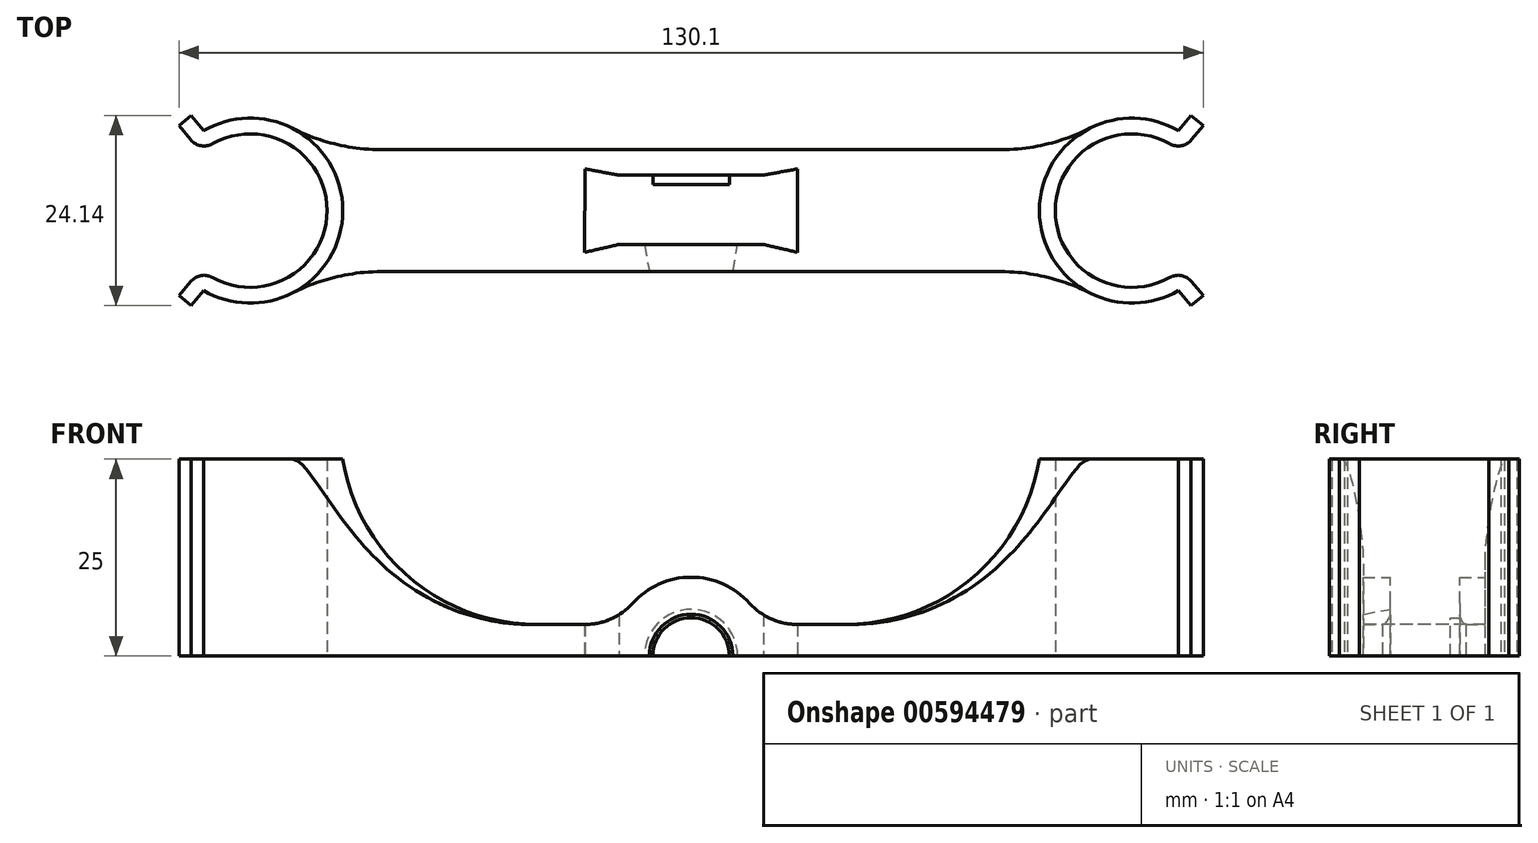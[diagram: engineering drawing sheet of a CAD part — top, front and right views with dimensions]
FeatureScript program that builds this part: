
annotation { "Feature Type Name" : "Feature", "Feature Type Description" : "" }
export const myFeature = defineFeature(function(context is Context, id is Id, definition is map)
    precondition{}
    {
        {
            var Q0;
            Q0=qCreatedBy(makeId("Top.planeOp"),FACE);
            var sketch = newSketch(context, id + "F0", { "sketchPlane" : qUnion([Q0])});
            skArc(sketch, "E0", {"start": v(-62.27, -7.47) * mm, "mid": v(-46.25, 0) * mm, "end": v(-62.27, 7.47) * mm});
            skLineSegment(sketch, "E1", {"start": v(-56, 0) * mm, "end": v(-68.54, -14.94) * mm, "construction": true});
            skLineSegment(sketch, "E2", {"start": v(-56, 0) * mm, "end": v(-67.56, 13.78) * mm, "construction": true});
            skArc(sketch, "E3", {"start": v(-63.55, -9) * mm, "mid": v(-44.25, 0) * mm, "end": v(-63.55, 9) * mm});
            skLineSegment(sketch, "E4", {"start": v(-63.55, 9) * mm, "end": v(-65.05, 10.78) * mm});
            skLineSegment(sketch, "E5", {"start": v(-65.05, 10.78) * mm, "end": v(-63.52, 12.07) * mm});
            skLineSegment(sketch, "E6", {"start": v(-63.52, 12.07) * mm, "end": v(-61.91, 10.16) * mm});
            skLineSegment(sketch, "E7", {"start": v(-54.18, 11.6) * mm, "end": v(-54.49, 9.63) * mm, "construction": true});
            skArc(sketch, "E8", {"start": v(-63.55, 9) * mm, "mid": v(-62.26, 8.25) * mm, "end": v(-60.78, 8.5) * mm});
            skLineSegment(sketch, "E9", {"start": v(-63.55, -9) * mm, "end": v(-65.05, -10.78) * mm});
            skLineSegment(sketch, "E10", {"start": v(-65.05, -10.78) * mm, "end": v(-63.52, -12.07) * mm});
            skLineSegment(sketch, "E11", {"start": v(-63.52, -12.07) * mm, "end": v(-61.91, -10.16) * mm});
            skArc(sketch, "E12", {"start": v(-60.78, -8.5) * mm, "mid": v(-62.26, -8.25) * mm, "end": v(-63.55, -9) * mm});
            skLineSegment(sketch, "E13.MirrorCS", {"start": v(65.05, -10.78) * mm, "end": v(63.52, -12.07) * mm});
            skLineSegment(sketch, "E14.MirrorCS", {"start": v(63.55, 9) * mm, "end": v(65.05, 10.78) * mm});
            skLineSegment(sketch, "E15.MirrorCS", {"start": v(63.52, -12.07) * mm, "end": v(61.91, -10.16) * mm});
            skLineSegment(sketch, "E16.MirrorCS", {"start": v(63.55, -9) * mm, "end": v(65.05, -10.78) * mm});
            skLineSegment(sketch, "E17.MirrorCS", {"start": v(65.05, 10.78) * mm, "end": v(63.52, 12.07) * mm});
            skLineSegment(sketch, "E18.MirrorCS", {"start": v(63.52, 12.07) * mm, "end": v(61.91, 10.16) * mm});
            skArc(sketch, "E19.MirrorCS", {"start": v(60.78, -8.5) * mm, "mid": v(62.26, -8.25) * mm, "end": v(63.55, -9) * mm});
            skArc(sketch, "E20.MirrorCS", {"start": v(63.55, 9) * mm, "mid": v(62.26, 8.25) * mm, "end": v(60.78, 8.5) * mm});
            skLineSegment(sketch, "E21.MirrorCS", {"start": v(54.18, 11.6) * mm, "end": v(54.49, 9.63) * mm, "construction": true});
            skArc(sketch, "E22.MirrorCS", {"start": v(62.27, -7.47) * mm, "mid": v(46.25, 0) * mm, "end": v(62.27, 7.47) * mm});
            skLineSegment(sketch, "E23.MirrorCS", {"start": v(56, 0) * mm, "end": v(68.54, -14.94) * mm, "construction": true});
            skLineSegment(sketch, "E24.MirrorCS", {"start": v(56, 0) * mm, "end": v(67.56, 13.78) * mm, "construction": true});
            skArc(sketch, "E25.MirrorCS", {"start": v(63.55, -9) * mm, "mid": v(44.25, 0) * mm, "end": v(63.55, 9) * mm});
            skSolve(sketch);
        }
        {
            var Q0;
            Q0=qSketchRegion(id+"F0",true);
            extrude(context, id + "F1", {"entities" : qUnion([Q0]), "depth" : 25 * mm});
        }
        {
            var Q0;
            Q0=qCreatedBy(makeId("Top.planeOp"),FACE);
            var sketch = newSketch(context, id + "F2", { "sketchPlane" : qUnion([Q0])});
            skLineSegment(sketch, "E26.bottom", {"start": v(50.08, -7.75) * mm, "end": v(-50.08, -7.75) * mm});
            skLineSegment(sketch, "E26.top", {"start": v(50.08, 7.75) * mm, "end": v(-50.08, 7.75) * mm});
            skLineSegment(sketch, "E26.left", {"start": v(50.08, -7.75) * mm, "end": v(50.08, 7.75) * mm});
            skLineSegment(sketch, "E26.right", {"start": v(-50.08, -7.75) * mm, "end": v(-50.08, 7.75) * mm});
            skPoint(sketch, "E26.middle", {"position": v(0, 0) * mm});
            skSolve(sketch);
        }
        {
            var Q0;
            Q0=qSketchRegion(id+"F2",true);
            extrude(context, id + "F3", {"entities" : qUnion([Q0]), "operationType" : NewBodyOperationType.ADD, "depth" : 4 * mm});
        }
        {
            var Q0;
            Q0=qCreatedBy(makeId("Top.planeOp"),FACE);
            var sketch = newSketch(context, id + "F4", { "sketchPlane" : qUnion([Q0])});
            skArc(sketch, "E27.0", {"start": v(-62.27, -7.47) * mm, "mid": v(-46.25, 0) * mm, "end": v(-62.27, 7.47) * mm});
            skArc(sketch, "E27.1", {"start": v(62.27, -7.47) * mm, "mid": v(46.25, 0) * mm, "end": v(62.27, 7.47) * mm});
            skLineSegment(sketch, "E28", {"start": v(-62.27, 7.47) * mm, "end": v(-62.27, -7.47) * mm});
            skLineSegment(sketch, "E29", {"start": v(62.27, 7.47) * mm, "end": v(62.27, -7.47) * mm});
            skSolve(sketch);
        }
        {
            var Q0;
            Q0=qSketchRegion(id+"F4",true);
            extrude(context, id + "F5", {"entities" : qUnion([Q0]), "operationType" : NewBodyOperationType.REMOVE, "endBound" : BoundingType.THROUGH_ALL, "depth" : 25 * mm});
        }
        {
            var Q0;
            Q0=qCreatedBy(makeId("Front.planeOp"),FACE);
            var sketch = newSketch(context, id + "F6", { "sketchPlane" : qUnion([Q0])});
            skArc(sketch, "E30", {"start": v(10, 0) * mm, "mid": v(0, 10) * mm, "end": v(-10, 0) * mm});
            skLineSegment(sketch, "E31.0", {"start": v(47.17, 0) * mm, "end": v(-47.17, 0) * mm});
            skSolve(sketch);
        }
        {
            var Q0;
            Q0=qSketchRegion(id+"F6",true);
            var Q1;
            Q1=makeQuery(id+"F3.opExtrude","SWEPT_FACE",FACE,{"disambiguationData":[OSD([sQuery(id+"F2.wireOp",EDGE,"E26.bottom")])]});
            var Q2;
            Q2=makeQuery(id+"F3.opExtrude","SWEPT_FACE",FACE,{"disambiguationData":[OSD([sQuery(id+"F2.wireOp",EDGE,"E26.top")])]});
            extrude(context, id + "F7", {"entities" : qUnion([Q0]), "operationType" : NewBodyOperationType.ADD, "endBound" : BoundingType.UP_TO_SURFACE, "endBoundEntityFace" : qUnion([Q1]), "depth" : 25 * mm, "hasSecondDirection" : true, "secondDirectionBound" : SecondDirectionBoundingType.UP_TO_SURFACE, "secondDirectionOppositeDirection" : true, "secondDirectionBoundEntityFace" : qUnion([Q2]), "secondDirectionDepth" : 25 * mm});
        }
        {
            var Q0;
            Q0=qCreatedBy(makeId("Top.planeOp"),FACE);
            var sketch = newSketch(context, id + "F8", { "sketchPlane" : qUnion([Q0])});
            skLineSegment(sketch, "E32.left", {"start": v(13.5, -5.3) * mm, "end": v(13.5, 5.3) * mm});
            skLineSegment(sketch, "E32.right", {"start": v(-13.5, -5.3) * mm, "end": v(-13.5, 5.3) * mm});
            skPoint(sketch, "E32.middle", {"position": v(0, 0) * mm});
            skLineSegment(sketch, "E33", {"start": v(9.17, 4.5) * mm, "end": v(-9.17, 4.5) * mm});
            skLineSegment(sketch, "E34", {"start": v(9.17, -4.3) * mm, "end": v(-9.17, -4.3) * mm});
            skLineSegment(sketch, "E35", {"start": v(-9.17, 4.5) * mm, "end": v(-13.5, 5.3) * mm});
            skLineSegment(sketch, "E36", {"start": v(-9.17, -4.3) * mm, "end": v(-13.5, -5.3) * mm});
            skLineSegment(sketch, "E37", {"start": v(9.17, 4.5) * mm, "end": v(13.5, 5.3) * mm});
            skLineSegment(sketch, "E38", {"start": v(9.17, -4.3) * mm, "end": v(13.5, -5.3) * mm});
            skPoint(sketch, "E39", {"position": v(-13.5, 0) * mm});
            skPoint(sketch, "E40", {"position": v(13.5, 0) * mm});
            skLineSegment(sketch, "E41.0", {"start": v(-9.17, -7.75) * mm, "end": v(-9.17, 7.75) * mm, "construction": true});
            skLineSegment(sketch, "E42.0", {"start": v(9.17, 7.75) * mm, "end": v(9.17, -7.75) * mm, "construction": true});
            skSolve(sketch);
        }
        {
            var Q0;
            Q0=qSketchRegion(id+"F8",true);
            extrude(context, id + "F9", {"entities" : qUnion([Q0]), "operationType" : NewBodyOperationType.REMOVE, "endBound" : BoundingType.THROUGH_ALL, "depth" : 8.6 * mm});
        }
        {
            var Q0;
            {var subQ0=sQuery(id+"F2.wireOp",EDGE,"E26.bottom");Q0=makeQuery(id+"F7.boolean.opBoolean","MERGE",FACE,{"derivedFrom":[makeQuery(id+"F3.opExtrude","SWEPT_FACE",FACE,{"disambiguationData":[OSD([subQ0])]}),makeQuery(id+"F7.opExtrude","CAP_FACE",FACE,{"disambiguationData":[OSD([subQ0])],"isStart":false})]});}
            var sketch = newSketch(context, id + "F10", { "sketchPlane" : qUnion([Q0])});
            skCircle(sketch, "E43", {"center": v(0, 0) * mm, "radius": 5.3 * mm});
            skSolve(sketch);
        }
        {
            var Q0;
            Q0=qSketchRegion(id+"F10",true);
            var Q1;
            Q1=makeQuery(id+"F9.boolean.opBoolean","COPY",FACE,{"derivedFrom":makeQuery(id+"F9.opExtrude","SWEPT_FACE",FACE,{"disambiguationData":[OSD([sQuery(id+"F8.wireOp",EDGE,"E34")])]})});
            extrude(context, id + "F11", {"entities" : qUnion([Q0]), "operationType" : NewBodyOperationType.REMOVE, "endBound" : BoundingType.UP_TO_SURFACE, "oppositeDirection" : true, "endBoundEntityFace" : qUnion([Q1]), "depth" : 25 * mm, "hasDraft" : true, "draftAngle" : 10 * degree});
        }
        {
            var Q0;
            Q0=makeQuery(id+"F9.boolean.opBoolean","COPY",FACE,{"derivedFrom":makeQuery(id+"F9.opExtrude","SWEPT_FACE",FACE,{"disambiguationData":[OSD([sQuery(id+"F8.wireOp",EDGE,"E33")])]})});
            var sketch = newSketch(context, id + "F12", { "sketchPlane" : qUnion([Q0])});
            skArc(sketch, "E44", {"start": v(4.85, 0) * mm, "mid": v(0, 4.85) * mm, "end": v(-4.85, 0) * mm});
            skLineSegment(sketch, "E45.0", {"start": v(9.17, 0) * mm, "end": v(-9.17, 0) * mm});
            skSolve(sketch);
        }
        {
            var Q0;
            Q0=qSketchRegion(id+"F12",true);
            extrude(context, id + "F13", {"entities" : qUnion([Q0]), "operationType" : NewBodyOperationType.ADD, "depth" : 1.2 * mm});
        }
        {
            var Q0;
            {var subQ0=makeQuery(id+"F7.opExtrude","SWEPT_FACE",FACE,{"disambiguationData":[OSD([sQuery(id+"F6.wireOp",EDGE,"E30")])]});var subQ1=sQuery(id+"F2.wireOp",EDGE,"E26.top");var subQ2=makeQuery(id+"F3.opExtrude","CAP_FACE",FACE,{"disambiguationData":[OSD([sQuery(id+"F2.wireOp",EDGE,"E26.bottom"),subQ1,sQuery(id+"F2.wireOp",EDGE,"E26.left"),sQuery(id+"F2.wireOp",EDGE,"E26.right")])],"isStart":false});Q0=makeQuery(id+"F9.boolean.opBoolean","SPLIT",EDGE,{"disambiguationData":[TD([makeQuery(id+"F3.opExtrude","SWEPT_FACE",FACE,{"disambiguationData":[OSD([subQ1])]})])],"derivedFrom":makeQuery(id+"F7.boolean.opBoolean","INTERSECT",EDGE,{"disambiguationData":[OD(1.0)],"derivedFrom":[subQ2,subQ0]})});}
            var Q1;
            {var subQ0=sQuery(id+"F2.wireOp",EDGE,"E26.bottom");var subQ1=makeQuery(id+"F3.opExtrude","CAP_FACE",FACE,{"disambiguationData":[OSD([subQ0,sQuery(id+"F2.wireOp",EDGE,"E26.top"),sQuery(id+"F2.wireOp",EDGE,"E26.left"),sQuery(id+"F2.wireOp",EDGE,"E26.right")])],"isStart":false});var subQ2=makeQuery(id+"F7.opExtrude","SWEPT_FACE",FACE,{"disambiguationData":[OSD([sQuery(id+"F6.wireOp",EDGE,"E30")])]});Q1=makeQuery(id+"F9.boolean.opBoolean","SPLIT",EDGE,{"disambiguationData":[TD([makeQuery(id+"F3.opExtrude","SWEPT_FACE",FACE,{"disambiguationData":[OSD([subQ0])]})])],"derivedFrom":makeQuery(id+"F7.boolean.opBoolean","INTERSECT",EDGE,{"disambiguationData":[OD(1.0)],"derivedFrom":[subQ1,subQ2]})});}
            var Q2;
            {var subQ0=sQuery(id+"F2.wireOp",EDGE,"E26.bottom");var subQ1=makeQuery(id+"F3.opExtrude","CAP_FACE",FACE,{"disambiguationData":[OSD([subQ0,sQuery(id+"F2.wireOp",EDGE,"E26.top"),sQuery(id+"F2.wireOp",EDGE,"E26.left"),sQuery(id+"F2.wireOp",EDGE,"E26.right")])],"isStart":false});var subQ2=makeQuery(id+"F7.opExtrude","SWEPT_FACE",FACE,{"disambiguationData":[OSD([sQuery(id+"F6.wireOp",EDGE,"E30")])]});Q2=makeQuery(id+"F9.boolean.opBoolean","SPLIT",EDGE,{"disambiguationData":[TD([makeQuery(id+"F3.opExtrude","SWEPT_FACE",FACE,{"disambiguationData":[OSD([subQ0])]})])],"derivedFrom":makeQuery(id+"F7.boolean.opBoolean","INTERSECT",EDGE,{"disambiguationData":[OD(0.0)],"derivedFrom":[subQ1,subQ2]})});}
            var Q3;
            {var subQ0=makeQuery(id+"F7.opExtrude","SWEPT_FACE",FACE,{"disambiguationData":[OSD([sQuery(id+"F6.wireOp",EDGE,"E30")])]});var subQ1=sQuery(id+"F2.wireOp",EDGE,"E26.top");var subQ2=makeQuery(id+"F3.opExtrude","CAP_FACE",FACE,{"disambiguationData":[OSD([sQuery(id+"F2.wireOp",EDGE,"E26.bottom"),subQ1,sQuery(id+"F2.wireOp",EDGE,"E26.left"),sQuery(id+"F2.wireOp",EDGE,"E26.right")])],"isStart":false});Q3=makeQuery(id+"F9.boolean.opBoolean","SPLIT",EDGE,{"disambiguationData":[TD([makeQuery(id+"F3.opExtrude","SWEPT_FACE",FACE,{"disambiguationData":[OSD([subQ1])]})])],"derivedFrom":makeQuery(id+"F7.boolean.opBoolean","INTERSECT",EDGE,{"disambiguationData":[OD(0.0)],"derivedFrom":[subQ2,subQ0]})});}
            fillet(context, id + "F14", {"entities" : qUnion([Q0, Q1, Q2, Q3]), "radius" : 8.1 * mm, "tangentPropagation" : true, "allowEdgeOverflow" : false});
        }
        {
            var Q0;
            Q0=makeQuery(id+"F3.boolean.opBoolean","INTERSECT",EDGE,{"derivedFrom":[makeQuery(id+"F1.opExtrude","SWEPT_FACE",FACE,{"disambiguationData":[OSD([sQuery(id+"F0.wireOp",EDGE,"E25.MirrorCS")])]}),makeQuery(id+"F3.opExtrude","CAP_FACE",FACE,{"disambiguationData":[OSD([sQuery(id+"F2.wireOp",EDGE,"E26.bottom"),sQuery(id+"F2.wireOp",EDGE,"E26.top"),sQuery(id+"F2.wireOp",EDGE,"E26.left"),sQuery(id+"F2.wireOp",EDGE,"E26.right")])],"isStart":false})]});
            var Q1;
            Q1=makeQuery(id+"F3.boolean.opBoolean","INTERSECT",EDGE,{"derivedFrom":[makeQuery(id+"F1.opExtrude","SWEPT_FACE",FACE,{"disambiguationData":[OSD([sQuery(id+"F0.wireOp",EDGE,"E3")])]}),makeQuery(id+"F3.opExtrude","CAP_FACE",FACE,{"disambiguationData":[OSD([sQuery(id+"F2.wireOp",EDGE,"E26.bottom"),sQuery(id+"F2.wireOp",EDGE,"E26.top"),sQuery(id+"F2.wireOp",EDGE,"E26.left"),sQuery(id+"F2.wireOp",EDGE,"E26.right")])],"isStart":false})]});
            fillet(context, id + "F15", {"entities" : qUnion([Q0, Q1]), "radius" : 25 * mm, "tangentPropagation" : true, "allowEdgeOverflow" : false});
        }
        {
            var Q0;
            Q0=makeQuery(id+"F3.boolean.opBoolean","INTERSECT",EDGE,{"derivedFrom":[makeQuery(id+"F1.opExtrude","SWEPT_FACE",FACE,{"disambiguationData":[OSD([sQuery(id+"F0.wireOp",EDGE,"E3")])]}),makeQuery(id+"F3.opExtrude","SWEPT_FACE",FACE,{"disambiguationData":[OSD([sQuery(id+"F2.wireOp",EDGE,"E26.bottom")])]})]});
            var Q1;
            Q1=makeQuery(id+"F3.boolean.opBoolean","INTERSECT",EDGE,{"derivedFrom":[makeQuery(id+"F1.opExtrude","SWEPT_FACE",FACE,{"disambiguationData":[OSD([sQuery(id+"F0.wireOp",EDGE,"E3")])]}),makeQuery(id+"F3.opExtrude","SWEPT_FACE",FACE,{"disambiguationData":[OSD([sQuery(id+"F2.wireOp",EDGE,"E26.top")])]})]});
            var Q2;
            Q2=makeQuery(id+"F3.boolean.opBoolean","INTERSECT",EDGE,{"derivedFrom":[makeQuery(id+"F1.opExtrude","SWEPT_FACE",FACE,{"disambiguationData":[OSD([sQuery(id+"F0.wireOp",EDGE,"E25.MirrorCS")])]}),makeQuery(id+"F3.opExtrude","SWEPT_FACE",FACE,{"disambiguationData":[OSD([sQuery(id+"F2.wireOp",EDGE,"E26.top")])]})]});
            var Q3;
            Q3=makeQuery(id+"F3.boolean.opBoolean","INTERSECT",EDGE,{"derivedFrom":[makeQuery(id+"F1.opExtrude","SWEPT_FACE",FACE,{"disambiguationData":[OSD([sQuery(id+"F0.wireOp",EDGE,"E25.MirrorCS")])]}),makeQuery(id+"F3.opExtrude","SWEPT_FACE",FACE,{"disambiguationData":[OSD([sQuery(id+"F2.wireOp",EDGE,"E26.bottom")])]})]});
            fillet(context, id + "F16", {"entities" : qUnion([Q0, Q1, Q2, Q3]), "radius" : 25 * mm, "tangentPropagation" : true, "allowEdgeOverflow" : false});
        }
    });
